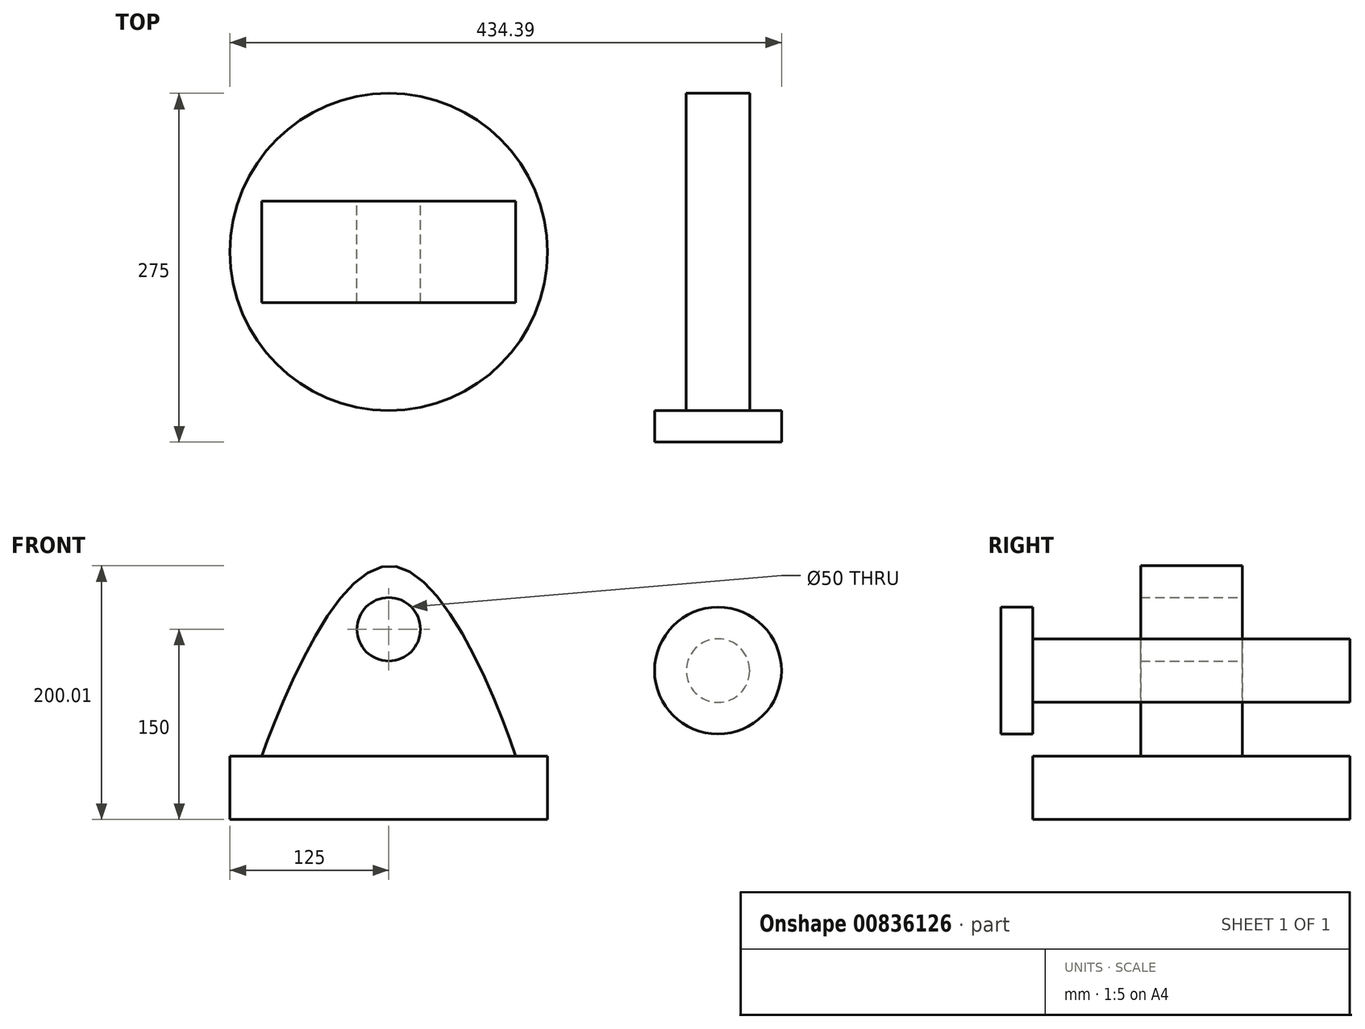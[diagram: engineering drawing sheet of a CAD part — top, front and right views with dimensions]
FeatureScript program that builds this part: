
annotation { "Feature Type Name" : "Feature", "Feature Type Description" : "" }
export const myFeature = defineFeature(function(context is Context, id is Id, definition is map)
    precondition{}
    {
        {
            var Q0;
            Q0=qCreatedBy(makeId("Front.planeOp"),FACE);
            var sketch = newSketch(context, id + "F0", { "sketchPlane" : qUnion([Q0])});
            skLineSegment(sketch, "E0", {"start": v(-100, 0) * mm, "end": v(100, 0) * mm});
            skFitSpline(sketch, "E1", {"points": [v(-100, 0) * mm, v(0, 150) * mm, v(100, 0) * mm], "startDerivative": vector(90, 249.73) * mm, "endDerivative": vector(90, -271.98) * mm});
            skLineSegment(sketch, "E2", {"start": v(-100, 0) * mm, "end": v(-100, -23.55) * mm});
            skLineSegment(sketch, "E3", {"start": v(100, 0) * mm, "end": v(100, -27.49) * mm});
            skCircle(sketch, "E4", {"center": v(0, 100) * mm, "radius": 25 * mm});
            skSolve(sketch);
        }
        {
            var Q0;
            Q0=makeQuery(id+"F0.imprint","IMPRINT",FACE,{"disambiguationData":[TD([[makeQuery(id+"F0.imprint","IMPRINT",EDGE,{"derivedFrom":sQuery(id+"F0.wireOp",EDGE,"E0")}),1.0]])]});
            extrude(context, id + "F1", {"entities" : qUnion([Q0]), "endBound" : BoundingType.SYMMETRIC, "depth" : 80 * mm, "offsetDistance" : 25 * mm});
        }
        {
            var Q0;
            Q0=makeQuery(id+"F1.opExtrude","SWEPT_FACE",FACE,{"disambiguationData":[OSD([sQuery(id+"F0.wireOp",EDGE,"E0")])]});
            var sketch = newSketch(context, id + "F2", { "sketchPlane" : qUnion([Q0])});
            skCircle(sketch, "E5", {"center": v(0, 0) * mm, "radius": 125 * mm});
            skSolve(sketch);
        }
        {
            var Q0;
            Q0=makeQuery(id+"F2.imprint","IMPRINT",FACE,{"disambiguationData":[TD([[makeQuery(id+"F2.imprint","IMPRINT",EDGE,{"derivedFrom":sQuery(id+"F2.wireOp",EDGE,"E5")}),1.0]])]});
            var Q1;
            {var subQ1=sQuery(id+"F0.wireOp",EDGE,"E0");Q1=makeQuery(id+"F2.imprint","IMPRINT",FACE,{"disambiguationData":[TD([[makeQuery(id+"F2.imprint","IMPRINT",EDGE,{"derivedFrom":makeQuery(id+"F1.opExtrude","CAP_EDGE",EDGE,{"disambiguationData":[OSD([subQ1])],"isStart":true})}),1.0]])]});}
            extrude(context, id + "F3", {"entities" : qUnion([Q0, Q1]), "operationType" : NewBodyOperationType.ADD, "depth" : 50 * mm, "offsetDistance" : 25 * mm});
        }
        {
            var Q0;
            Q0=qCreatedBy(makeId("Front.planeOp"),FACE);
            var sketch = newSketch(context, id + "F4", { "sketchPlane" : qUnion([Q0])});
            skCircle(sketch, "E6", {"center": v(259.4, 67.4) * mm, "radius": 25 * mm});
            skSolve(sketch);
        }
        {
            var Q0;
            Q0 = qSketchRegion(id + "F4", true);
            extrude(context, id + "F5", {"entities" : qUnion([Q0]), "endBound" : BoundingType.SYMMETRIC, "depth" : 250 * mm, "offsetDistance" : 25 * mm});
        }
        {
            var Q0;
            Q0=makeQuery(id+"F5.opExtrude","CAP_FACE",FACE,{"disambiguationData":[OSD([sQuery(id+"F4.wireOp",EDGE,"E6")])],"isStart":false});
            var sketch = newSketch(context, id + "F6", { "sketchPlane" : qUnion([Q0])});
            skCircle(sketch, "E7", {"center": v(259.4, 67.4) * mm, "radius": 50 * mm});
            skSolve(sketch);
        }
        {
            var Q0;
            Q0 = qSketchRegion(id + "F6", true);
            extrude(context, id + "F7", {"entities" : qUnion([Q0]), "operationType" : NewBodyOperationType.ADD, "depth" : 25 * mm, "offsetDistance" : 25 * mm});
        }
    });
